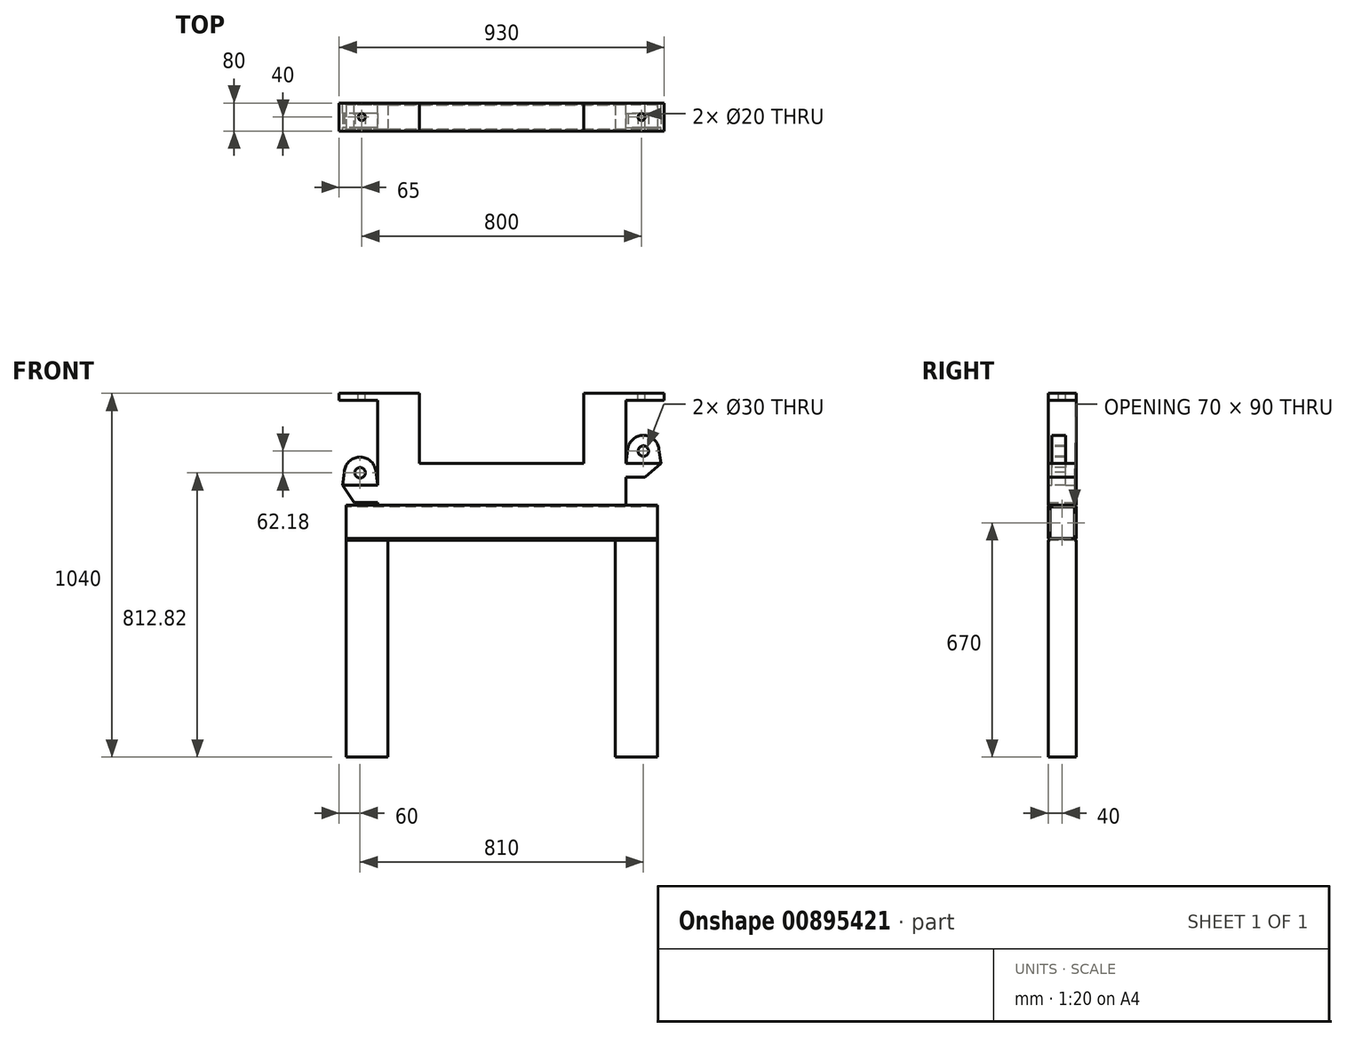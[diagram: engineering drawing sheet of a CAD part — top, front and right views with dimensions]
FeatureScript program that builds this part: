
annotation { "Feature Type Name" : "Feature", "Feature Type Description" : "" }
export const myFeature = defineFeature(function(context is Context, id is Id, definition is map)
    precondition{}
    {
        {
            var Q0;
            Q0=qCreatedBy(makeId("Front.planeOp"),FACE);
            var sketch = newSketch(context, id + "F0", { "sketchPlane" : qUnion([Q0])});
            skLineSegment(sketch, "E0.bottom", {"start": v(-355, 0) * mm, "end": v(-235, 0) * mm});
            skLineSegment(sketch, "E0.top", {"start": v(-355, -1040) * mm, "end": v(-235, -1040) * mm});
            skLineSegment(sketch, "E0.left", {"start": v(-355, -20) * mm, "end": v(-355, -262.18) * mm});
            skLineSegment(sketch, "E0.right", {"start": v(355, -20) * mm, "end": v(355, -200) * mm});
            skLineSegment(sketch, "E1.top", {"start": v(-235, -840) * mm, "end": v(235, -840) * mm});
            skLineSegment(sketch, "E1.left", {"start": v(-235, -1040) * mm, "end": v(-235, -840) * mm});
            skLineSegment(sketch, "E1.right", {"start": v(235, -1040) * mm, "end": v(235, -840) * mm});
            skLineSegment(sketch, "E2.bottom", {"start": v(-235, -720) * mm, "end": v(235, -720) * mm});
            skLineSegment(sketch, "E2.top", {"start": v(-235, -320) * mm, "end": v(235, -320) * mm});
            skLineSegment(sketch, "E2.left", {"start": v(-235, -720) * mm, "end": v(-235, -320) * mm});
            skLineSegment(sketch, "E2.right", {"start": v(235, -720) * mm, "end": v(235, -320) * mm});
            skLineSegment(sketch, "E3.bottom", {"start": v(-235, -200) * mm, "end": v(235, -200) * mm});
            skLineSegment(sketch, "E3.left", {"start": v(-235, -200) * mm, "end": v(-235, 0) * mm});
            skLineSegment(sketch, "E3.right", {"start": v(235, -200) * mm, "end": v(235, 0) * mm});
            skLineSegment(sketch, "E4.bottom", {"start": v(-355, 0) * mm, "end": v(-465, 0) * mm});
            skLineSegment(sketch, "E4.top", {"start": v(-355, -20) * mm, "end": v(-465, -20) * mm});
            skLineSegment(sketch, "E4.right", {"start": v(-465, 0) * mm, "end": v(-465, -20) * mm});
            skLineSegment(sketch, "E5.bottom", {"start": v(355, 0) * mm, "end": v(465, 0) * mm});
            skLineSegment(sketch, "E5.top", {"start": v(355, -20) * mm, "end": v(465, -20) * mm});
            skLineSegment(sketch, "E5.right", {"start": v(465, 0) * mm, "end": v(465, -20) * mm});
            skLineSegment(sketch, "E6.bottom", {"start": v(355, -1040) * mm, "end": v(415, -1040) * mm});
            skLineSegment(sketch, "E6.top", {"start": v(355, -1020) * mm, "end": v(415, -1020) * mm});
            skLineSegment(sketch, "E6.left", {"start": v(355, -1040) * mm, "end": v(355, -1020) * mm});
            skLineSegment(sketch, "E6.right", {"start": v(415, -1040) * mm, "end": v(415, -1020) * mm});
            skLineSegment(sketch, "E7.bottom", {"start": v(-355, -1040) * mm, "end": v(-415, -1040) * mm});
            skLineSegment(sketch, "E7.top", {"start": v(-355, -1020) * mm, "end": v(-415, -1020) * mm});
            skLineSegment(sketch, "E7.left", {"start": v(-355, -1040) * mm, "end": v(-355, -1020) * mm});
            skLineSegment(sketch, "E7.right", {"start": v(-415, -1040) * mm, "end": v(-415, -1020) * mm});
            skLineSegment(sketch, "E8.trimOffspring", {"start": v(235, 0) * mm, "end": v(355, 0) * mm});
            skLineSegment(sketch, "E9.trimOffspring", {"start": v(235, -1040) * mm, "end": v(355, -1040) * mm});
            skLineSegment(sketch, "E10.bottom", {"start": v(-355, -312.18) * mm, "end": v(-421.83, -312.18) * mm});
            skLineSegment(sketch, "E10.top", {"start": v(-355, -262.18) * mm, "end": v(-455, -262.18) * mm});
            skLineSegment(sketch, "E11", {"start": v(-455, -262.18) * mm, "end": v(-421.83, -312.18) * mm});
            skLineSegment(sketch, "E12.bottom", {"start": v(355, -200) * mm, "end": v(455, -200) * mm});
            skLineSegment(sketch, "E12.top", {"start": v(355, -240) * mm, "end": v(410.28, -240) * mm});
            skLineSegment(sketch, "E13", {"start": v(455, -200) * mm, "end": v(410.28, -240) * mm});
            skLineSegment(sketch, "E14.trimOffspring", {"start": v(-355, -312.18) * mm, "end": v(-355, -1040) * mm});
            skLineSegment(sketch, "E15.trimOffspring", {"start": v(355, -240) * mm, "end": v(355, -1040) * mm});
            skSolve(sketch);
        }
        {
            var Q0;
            Q0=qSketchRegion(id+"F0",true);
            extrude(context, id + "F1", {"entities" : qUnion([Q0]), "depth" : 80 * mm, "offsetDistance" : 25 * mm});
        }
        {
            var Q0;
            Q0=makeQuery(id+"F1.opExtrude","CAP_FACE",FACE,{"disambiguationData":[OSD([sQuery(id+"F0.wireOp",EDGE,"E0.bottom"),sQuery(id+"F0.wireOp",EDGE,"E0.top"),sQuery(id+"F0.wireOp",EDGE,"E0.left"),sQuery(id+"F0.wireOp",EDGE,"E0.right"),sQuery(id+"F0.wireOp",EDGE,"E1.top"),sQuery(id+"F0.wireOp",EDGE,"E1.left"),sQuery(id+"F0.wireOp",EDGE,"E1.right"),sQuery(id+"F0.wireOp",EDGE,"E2.bottom"),sQuery(id+"F0.wireOp",EDGE,"E2.top"),sQuery(id+"F0.wireOp",EDGE,"E2.left"),sQuery(id+"F0.wireOp",EDGE,"E2.right"),sQuery(id+"F0.wireOp",EDGE,"E3.bottom"),sQuery(id+"F0.wireOp",EDGE,"E3.left"),sQuery(id+"F0.wireOp",EDGE,"E3.right"),sQuery(id+"F0.wireOp",EDGE,"E4.bottom"),sQuery(id+"F0.wireOp",EDGE,"E4.top"),sQuery(id+"F0.wireOp",EDGE,"E4.right"),sQuery(id+"F0.wireOp",EDGE,"E5.bottom"),sQuery(id+"F0.wireOp",EDGE,"E5.top"),sQuery(id+"F0.wireOp",EDGE,"E5.right"),sQuery(id+"F0.wireOp",EDGE,"E6.bottom"),sQuery(id+"F0.wireOp",EDGE,"E6.top"),sQuery(id+"F0.wireOp",EDGE,"E6.right"),sQuery(id+"F0.wireOp",EDGE,"E7.bottom"),sQuery(id+"F0.wireOp",EDGE,"E7.top"),sQuery(id+"F0.wireOp",EDGE,"E7.right"),sQuery(id+"F0.wireOp",EDGE,"E8.trimOffspring"),sQuery(id+"F0.wireOp",EDGE,"E9.trimOffspring"),sQuery(id+"F0.wireOp",EDGE,"E10.bottom"),sQuery(id+"F0.wireOp",EDGE,"E10.top"),sQuery(id+"F0.wireOp",EDGE,"E11"),sQuery(id+"F0.wireOp",EDGE,"E12.bottom"),sQuery(id+"F0.wireOp",EDGE,"E12.top"),sQuery(id+"F0.wireOp",EDGE,"E13"),sQuery(id+"F0.wireOp",EDGE,"E14.trimOffspring"),sQuery(id+"F0.wireOp",EDGE,"E15.trimOffspring")])],"isStart":false});
            var sketch = newSketch(context, id + "F2", { "sketchPlane" : qUnion([Q0])});
            skLineSegment(sketch, "E16.bottom", {"start": v(-451.7, -1040) * mm, "end": v(537.4, -1040) * mm});
            skLineSegment(sketch, "E16.top", {"start": v(-451.7, -320) * mm, "end": v(537.4, -320) * mm});
            skLineSegment(sketch, "E16.left", {"start": v(-451.7, -1040) * mm, "end": v(-451.7, -320) * mm});
            skLineSegment(sketch, "E16.right", {"start": v(537.4, -1040) * mm, "end": v(537.4, -320) * mm});
            skSolve(sketch);
        }
        {
            var Q0;
            Q0=qSketchRegion(id+"F2",true);
            extrude(context, id + "F3", {"entities" : qUnion([Q0]), "operationType" : NewBodyOperationType.REMOVE, "oppositeDirection" : true, "depth" : 80 * mm, "offsetDistance" : 25 * mm});
        }
        {
            var Q0;
            Q0=makeQuery(id+"F1.opExtrude","SWEPT_FACE",FACE,{"disambiguationData":[OSD([sQuery(id+"F0.wireOp",EDGE,"E0.bottom"),sQuery(id+"F0.wireOp",EDGE,"E4.bottom")])]});
            var sketch = newSketch(context, id + "F4", { "sketchPlane" : qUnion([Q0])});
            skCircle(sketch, "E17", {"center": v(-400, -40) * mm, "radius": 10 * mm});
            skCircle(sketch, "E18", {"center": v(400, -40) * mm, "radius": 10 * mm});
            skSolve(sketch);
        }
        {
            var Q0;
            Q0=qSketchRegion(id+"F4",true);
            extrude(context, id + "F5", {"entities" : qUnion([Q0]), "operationType" : NewBodyOperationType.REMOVE, "oppositeDirection" : true, "depth" : 25 * mm, "offsetDistance" : 25 * mm});
        }
        {
            var Q0;
            Q0=makeQuery(id+"F1.opExtrude","CAP_FACE",FACE,{"disambiguationData":[OSD([sQuery(id+"F0.wireOp",EDGE,"E0.bottom"),sQuery(id+"F0.wireOp",EDGE,"E0.top"),sQuery(id+"F0.wireOp",EDGE,"E0.left"),sQuery(id+"F0.wireOp",EDGE,"E0.right"),sQuery(id+"F0.wireOp",EDGE,"E1.top"),sQuery(id+"F0.wireOp",EDGE,"E1.left"),sQuery(id+"F0.wireOp",EDGE,"E1.right"),sQuery(id+"F0.wireOp",EDGE,"E2.bottom"),sQuery(id+"F0.wireOp",EDGE,"E2.top"),sQuery(id+"F0.wireOp",EDGE,"E2.left"),sQuery(id+"F0.wireOp",EDGE,"E2.right"),sQuery(id+"F0.wireOp",EDGE,"E3.bottom"),sQuery(id+"F0.wireOp",EDGE,"E3.left"),sQuery(id+"F0.wireOp",EDGE,"E3.right"),sQuery(id+"F0.wireOp",EDGE,"E4.bottom"),sQuery(id+"F0.wireOp",EDGE,"E4.top"),sQuery(id+"F0.wireOp",EDGE,"E4.right"),sQuery(id+"F0.wireOp",EDGE,"E5.bottom"),sQuery(id+"F0.wireOp",EDGE,"E5.top"),sQuery(id+"F0.wireOp",EDGE,"E5.right"),sQuery(id+"F0.wireOp",EDGE,"E6.bottom"),sQuery(id+"F0.wireOp",EDGE,"E6.top"),sQuery(id+"F0.wireOp",EDGE,"E6.right"),sQuery(id+"F0.wireOp",EDGE,"E7.bottom"),sQuery(id+"F0.wireOp",EDGE,"E7.top"),sQuery(id+"F0.wireOp",EDGE,"E7.right"),sQuery(id+"F0.wireOp",EDGE,"E8.trimOffspring"),sQuery(id+"F0.wireOp",EDGE,"E9.trimOffspring"),sQuery(id+"F0.wireOp",EDGE,"E10.bottom"),sQuery(id+"F0.wireOp",EDGE,"E10.top"),sQuery(id+"F0.wireOp",EDGE,"E11"),sQuery(id+"F0.wireOp",EDGE,"E12.bottom"),sQuery(id+"F0.wireOp",EDGE,"E12.top"),sQuery(id+"F0.wireOp",EDGE,"E13"),sQuery(id+"F0.wireOp",EDGE,"E14.trimOffspring"),sQuery(id+"F0.wireOp",EDGE,"E15.trimOffspring")])],"isStart":false});
            var sketch = newSketch(context, id + "F6", { "sketchPlane" : qUnion([Q0])});
            skArc(sketch, "E19", {"start": v(-360.39, -221.3) * mm, "mid": v(-407.1, -182.23) * mm, "end": v(-449.97, -225.48) * mm});
            skLineSegment(sketch, "E20", {"start": v(-455, -262.18) * mm, "end": v(-449.97, -225.48) * mm});
            skLineSegment(sketch, "E21", {"start": v(-355, -262.18) * mm, "end": v(-360.39, -221.3) * mm});
            skCircle(sketch, "E22", {"center": v(-405, -227.18) * mm, "radius": 15 * mm});
            skArc(sketch, "E23", {"start": v(449.61, -159.12) * mm, "mid": v(408.68, -120.15) * mm, "end": v(361.94, -151.93) * mm});
            skPoint(sketch, "E23.centerSnap0", {"position": v(405, -200) * mm});
            skLineSegment(sketch, "E24", {"start": v(455, -200) * mm, "end": v(449.61, -159.12) * mm});
            skLineSegment(sketch, "E25", {"start": v(355, -200) * mm, "end": v(361.94, -151.93) * mm});
            skCircle(sketch, "E26", {"center": v(405, -165) * mm, "radius": 15 * mm});
            skSolve(sketch);
        }
        {
            var Q0;
            Q0=makeQuery(id+"F6.imprint","IMPRINT",FACE,{"disambiguationData":[TD([[makeQuery(id+"F6.imprint","IMPRINT",EDGE,{"derivedFrom":sQuery(id+"F6.wireOp",EDGE,"E19")}),1.0]])]});
            var Q1;
            Q1=makeQuery(id+"F6.imprint","IMPRINT",FACE,{"disambiguationData":[TD([[makeQuery(id+"F6.imprint","IMPRINT",EDGE,{"derivedFrom":sQuery(id+"F6.wireOp",EDGE,"E23")}),1.0]])]});
            extrude(context, id + "F7", {"entities" : qUnion([Q0, Q1]), "operationType" : NewBodyOperationType.ADD, "oppositeDirection" : true, "depth" : 50 * mm, "offsetDistance" : 25 * mm, "hasSecondDirection" : true, "secondDirectionOppositeDirection" : true, "secondDirectionDepth" : 10 * mm});
        }
        {
            var Q0;
            {var subQ0=sQuery(id+"F0.wireOp",EDGE,"E12.bottom");var subQ1=sQuery(id+"F0.wireOp",EDGE,"E10.top");Q0=makeQuery(id+"F7.boolean.opBoolean","MERGE",FACE,{"derivedFrom":[makeQuery(id+"F1.opExtrude","CAP_FACE",FACE,{"disambiguationData":[OSD([sQuery(id+"F0.wireOp",EDGE,"E0.bottom"),sQuery(id+"F0.wireOp",EDGE,"E0.top"),sQuery(id+"F0.wireOp",EDGE,"E0.left"),sQuery(id+"F0.wireOp",EDGE,"E0.right"),sQuery(id+"F0.wireOp",EDGE,"E1.top"),sQuery(id+"F0.wireOp",EDGE,"E1.left"),sQuery(id+"F0.wireOp",EDGE,"E1.right"),sQuery(id+"F0.wireOp",EDGE,"E2.bottom"),sQuery(id+"F0.wireOp",EDGE,"E2.top"),sQuery(id+"F0.wireOp",EDGE,"E2.left"),sQuery(id+"F0.wireOp",EDGE,"E2.right"),sQuery(id+"F0.wireOp",EDGE,"E3.bottom"),sQuery(id+"F0.wireOp",EDGE,"E3.left"),sQuery(id+"F0.wireOp",EDGE,"E3.right"),sQuery(id+"F0.wireOp",EDGE,"E4.bottom"),sQuery(id+"F0.wireOp",EDGE,"E4.top"),sQuery(id+"F0.wireOp",EDGE,"E4.right"),sQuery(id+"F0.wireOp",EDGE,"E5.bottom"),sQuery(id+"F0.wireOp",EDGE,"E5.top"),sQuery(id+"F0.wireOp",EDGE,"E5.right"),sQuery(id+"F0.wireOp",EDGE,"E6.bottom"),sQuery(id+"F0.wireOp",EDGE,"E6.top"),sQuery(id+"F0.wireOp",EDGE,"E6.right"),sQuery(id+"F0.wireOp",EDGE,"E7.bottom"),sQuery(id+"F0.wireOp",EDGE,"E7.top"),sQuery(id+"F0.wireOp",EDGE,"E7.right"),sQuery(id+"F0.wireOp",EDGE,"E8.trimOffspring"),sQuery(id+"F0.wireOp",EDGE,"E9.trimOffspring"),sQuery(id+"F0.wireOp",EDGE,"E10.bottom"),subQ1,sQuery(id+"F0.wireOp",EDGE,"E11"),subQ0,sQuery(id+"F0.wireOp",EDGE,"E12.top"),sQuery(id+"F0.wireOp",EDGE,"E13"),sQuery(id+"F0.wireOp",EDGE,"E14.trimOffspring"),sQuery(id+"F0.wireOp",EDGE,"E15.trimOffspring")])],"isStart":false}),makeQuery(id+"F7.opExtrude","CAP_FACE",FACE,{"disambiguationData":[OSD([subQ1,sQuery(id+"F6.wireOp",EDGE,"E19"),sQuery(id+"F6.wireOp",EDGE,"E20"),sQuery(id+"F6.wireOp",EDGE,"E21"),sQuery(id+"F6.wireOp",EDGE,"E22")])],"isStart":true}),makeQuery(id+"F7.opExtrude","CAP_FACE",FACE,{"disambiguationData":[OSD([subQ0,sQuery(id+"F6.wireOp",EDGE,"E23"),sQuery(id+"F6.wireOp",EDGE,"E24"),sQuery(id+"F6.wireOp",EDGE,"E25"),sQuery(id+"F6.wireOp",EDGE,"E26")])],"isStart":true})]});}
            var sketch = newSketch(context, id + "F8", { "sketchPlane" : qUnion([Q0])});
            skLineSegment(sketch, "E27.bottom", {"start": v(325, -380) * mm, "end": v(-325, -380) * mm});
            skLineSegment(sketch, "E27.top", {"start": v(-325, -1040) * mm, "end": v(325, -1040) * mm});
            skLineSegment(sketch, "E27.left", {"start": v(-325, -380) * mm, "end": v(-325, -1040) * mm});
            skLineSegment(sketch, "E27.right", {"start": v(325, -380) * mm, "end": v(325, -1040) * mm});
            skSolve(sketch);
        }
        {
            var Q0;
            Q0=makeQuery(id+"F8.imprint","IMPRINT",FACE,{"disambiguationData":[TD([[makeQuery(id+"F8.imprint","IMPRINT",EDGE,{"derivedFrom":makeQuery(id+"F1.opExtrude","CAP_EDGE",EDGE,{"disambiguationData":[OSD([sQuery(id+"F0.wireOp",EDGE,"E0.left")])],"isStart":false})}),1.0]])]});
            var sketch = newSketch(context, id + "F9", { "sketchPlane" : qUnion([Q0])});
            skLineSegment(sketch, "E28.bottom", {"start": v(-445, -320) * mm, "end": v(445, -320) * mm});
            skLineSegment(sketch, "E28.top", {"start": v(-325, -420) * mm, "end": v(325, -420) * mm});
            skLineSegment(sketch, "E28.left", {"start": v(-445, -320) * mm, "end": v(-445, -420) * mm});
            skLineSegment(sketch, "E28.right", {"start": v(445, -320) * mm, "end": v(445, -420) * mm});
            skLineSegment(sketch, "E29.top", {"start": v(-445, -1040) * mm, "end": v(-325, -1040) * mm});
            skLineSegment(sketch, "E29.left", {"start": v(-445, -420) * mm, "end": v(-445, -1040) * mm});
            skLineSegment(sketch, "E29.right", {"start": v(-325, -420) * mm, "end": v(-325, -1040) * mm});
            skLineSegment(sketch, "E30.top", {"start": v(445, -1040) * mm, "end": v(325, -1040) * mm});
            skLineSegment(sketch, "E30.left", {"start": v(445, -420) * mm, "end": v(445, -1040) * mm});
            skLineSegment(sketch, "E30.right", {"start": v(325, -420) * mm, "end": v(325, -1040) * mm});
            skSolve(sketch);
        }
        {
            var Q0;
            Q0 = qSketchRegion(id + "F9", true);
            extrude(context, id + "F10", {"entities" : qUnion([Q0]), "operationType" : NewBodyOperationType.ADD, "oppositeDirection" : true, "depth" : 80 * mm, "offsetDistance" : 25 * mm});
        }
        {
            var Q0;
            Q0=makeQuery(id+"F10.opExtrude","SWEPT_FACE",FACE,{"disambiguationData":[OSD([sQuery(id+"F9.wireOp",EDGE,"E28.left"),sQuery(id+"F9.wireOp",EDGE,"E29.left")])]});
            var sketch = newSketch(context, id + "F11", { "sketchPlane" : qUnion([Q0])});
            skLineSegment(sketch, "E31.bottom", {"start": v(10, -325) * mm, "end": v(70, -325) * mm});
            skLineSegment(sketch, "E31.top", {"start": v(10, -415) * mm, "end": v(70, -415) * mm});
            skLineSegment(sketch, "E31.left", {"start": v(5, -330) * mm, "end": v(5, -410) * mm});
            skLineSegment(sketch, "E31.right", {"start": v(75, -330) * mm, "end": v(75, -410) * mm});
            skPoint(sketch, "E32.visualSharp", {"position": v(5, -325) * mm});
            skArc(sketch, "E32.filletArc", {"start": v(10, -325) * mm, "mid": v(6.46, -326.46) * mm, "end": v(5, -330) * mm});
            skPoint(sketch, "E33.visualSharp", {"position": v(75, -325) * mm});
            skArc(sketch, "E33.filletArc", {"start": v(75, -330) * mm, "mid": v(73.54, -326.46) * mm, "end": v(70, -325) * mm});
            skPoint(sketch, "E34.visualSharp", {"position": v(75, -415) * mm});
            skArc(sketch, "E34.filletArc", {"start": v(70, -415) * mm, "mid": v(73.54, -413.54) * mm, "end": v(75, -410) * mm});
            skPoint(sketch, "E35.visualSharp", {"position": v(5, -415) * mm});
            skArc(sketch, "E35.filletArc", {"start": v(5, -410) * mm, "mid": v(6.46, -413.54) * mm, "end": v(10, -415) * mm});
            skSolve(sketch);
        }
        {
            var Q0;
            Q0=makeQuery(id+"F11.imprint","IMPRINT",FACE,{"disambiguationData":[TD([[makeQuery(id+"F11.imprint","IMPRINT",EDGE,{"derivedFrom":sQuery(id+"F11.wireOp",EDGE,"E31.bottom")}),-1.0]])]});
            extrude(context, id + "F12", {"entities" : qUnion([Q0]), "operationType" : NewBodyOperationType.REMOVE, "oppositeDirection" : true, "depth" : 890 * mm, "offsetDistance" : 25 * mm});
        }
        {
            var Q0;
            {var subQ2=sQuery(id+"F9.wireOp",EDGE,"E28.bottom");var subQ3=sQuery(id+"F0.wireOp",EDGE,"E14.trimOffspring");Q0=makeQuery(id+"F10.boolean.opBoolean","SPLIT",EDGE,{"disambiguationData":[TD([makeQuery(id+"F1.opExtrude","SWEPT_FACE",FACE,{"disambiguationData":[OSD([subQ3])]})])],"derivedFrom":makeQuery(id+"F10.opExtrude","CAP_EDGE",EDGE,{"disambiguationData":[OSD([subQ2])],"isStart":true})});}
            var Q1;
            {var subQ0=sQuery(id+"F9.wireOp",EDGE,"E28.bottom");var subQ1=sQuery(id+"F0.wireOp",EDGE,"E14.trimOffspring");Q1=makeQuery(id+"F10.boolean.opBoolean","SPLIT",EDGE,{"disambiguationData":[TD([makeQuery(id+"F1.opExtrude","SWEPT_FACE",FACE,{"disambiguationData":[OSD([subQ1])]})])],"derivedFrom":makeQuery(id+"F10.opExtrude","CAP_EDGE",EDGE,{"disambiguationData":[OSD([subQ0])],"isStart":false})});}
            var Q2;
            Q2=makeQuery(id+"F10.opExtrude","CAP_EDGE",EDGE,{"disambiguationData":[OSD([sQuery(id+"F9.wireOp",EDGE,"E28.top")])],"isStart":true});
            var Q3;
            Q3=makeQuery(id+"F10.opExtrude","CAP_EDGE",EDGE,{"disambiguationData":[OSD([sQuery(id+"F9.wireOp",EDGE,"E28.top")])],"isStart":false});
            var Q4;
            {var subQ2=sQuery(id+"F9.wireOp",EDGE,"E28.bottom");var subQ3=sQuery(id+"F0.wireOp",EDGE,"E15.trimOffspring");Q4=makeQuery(id+"F10.boolean.opBoolean","SPLIT",EDGE,{"disambiguationData":[TD([makeQuery(id+"F1.opExtrude","SWEPT_FACE",FACE,{"disambiguationData":[OSD([subQ3])]})])],"derivedFrom":makeQuery(id+"F10.opExtrude","CAP_EDGE",EDGE,{"disambiguationData":[OSD([subQ2])],"isStart":true})});}
            var Q5;
            {var subQ0=sQuery(id+"F9.wireOp",EDGE,"E28.bottom");var subQ1=sQuery(id+"F0.wireOp",EDGE,"E15.trimOffspring");Q5=makeQuery(id+"F10.boolean.opBoolean","SPLIT",EDGE,{"disambiguationData":[TD([makeQuery(id+"F1.opExtrude","SWEPT_FACE",FACE,{"disambiguationData":[OSD([subQ1])]})])],"derivedFrom":makeQuery(id+"F10.opExtrude","CAP_EDGE",EDGE,{"disambiguationData":[OSD([subQ0])],"isStart":false})});}
            fillet(context, id + "F13", {"entities" : qUnion([Q0, Q1, Q2, Q3, Q4, Q5]), "radius" : 5 * mm, "tangentPropagation" : true, "allowEdgeOverflow" : false});
        }
        {
            var Q0;
            Q0=makeQuery(id+"F10.opExtrude","SWEPT_FACE",FACE,{"disambiguationData":[OSD([sQuery(id+"F9.wireOp",EDGE,"E28.left"),sQuery(id+"F9.wireOp",EDGE,"E29.left")])]});
            var sketch = newSketch(context, id + "F14", { "sketchPlane" : qUnion([Q0])});
            skLineSegment(sketch, "E36", {"start": v(80, -420) * mm, "end": v(75, -420) * mm});
            skLineSegment(sketch, "E37", {"start": v(75, -420) * mm, "end": v(80, -415) * mm});
            skLineSegment(sketch, "E38", {"start": v(80, -415) * mm, "end": v(80, -420) * mm});
            skLineSegment(sketch, "E39", {"start": v(0, -420) * mm, "end": v(5, -420) * mm});
            skLineSegment(sketch, "E40", {"start": v(5, -420) * mm, "end": v(0, -415) * mm});
            skLineSegment(sketch, "E41", {"start": v(0, -415) * mm, "end": v(0, -420) * mm});
            skSolve(sketch);
        }
        {
            var Q0;
            Q0 = qSketchRegion(id + "F14", true);
            extrude(context, id + "F15", {"entities" : qUnion([Q0]), "operationType" : NewBodyOperationType.REMOVE, "oppositeDirection" : true, "depth" : 890 * mm, "offsetDistance" : 25 * mm});
        }
        {
            var Q0;
            Q0=makeQuery(id+"F10.opExtrude","SWEPT_FACE",FACE,{"disambiguationData":[OSD([sQuery(id+"F9.wireOp",EDGE,"E28.left"),sQuery(id+"F9.wireOp",EDGE,"E29.left")])]});
            var sketch = newSketch(context, id + "F16", { "sketchPlane" : qUnion([Q0])});
            skArc(sketch, "E42.0", {"start": v(80, -325) * mm, "mid": v(78.54, -321.46) * mm, "end": v(75, -320) * mm});
            skArc(sketch, "E43.0", {"start": v(5, -320) * mm, "mid": v(1.46, -321.46) * mm, "end": v(0, -325) * mm});
            skLineSegment(sketch, "E44.0", {"start": v(80, -312.18) * mm, "end": v(80, -325) * mm});
            skLineSegment(sketch, "E45.0", {"start": v(0, -312.18) * mm, "end": v(0, -325) * mm});
            skLineSegment(sketch, "E46", {"start": v(5, -320) * mm, "end": v(0, -320) * mm});
            skLineSegment(sketch, "E47", {"start": v(75, -320) * mm, "end": v(80, -320) * mm});
            skSolve(sketch);
        }
        {
            var Q0;
            Q0 = qSketchRegion(id + "F16", true);
            extrude(context, id + "F17", {"entities" : qUnion([Q0]), "operationType" : NewBodyOperationType.REMOVE, "oppositeDirection" : true, "depth" : 890 * mm, "offsetDistance" : 25 * mm});
        }
    });
